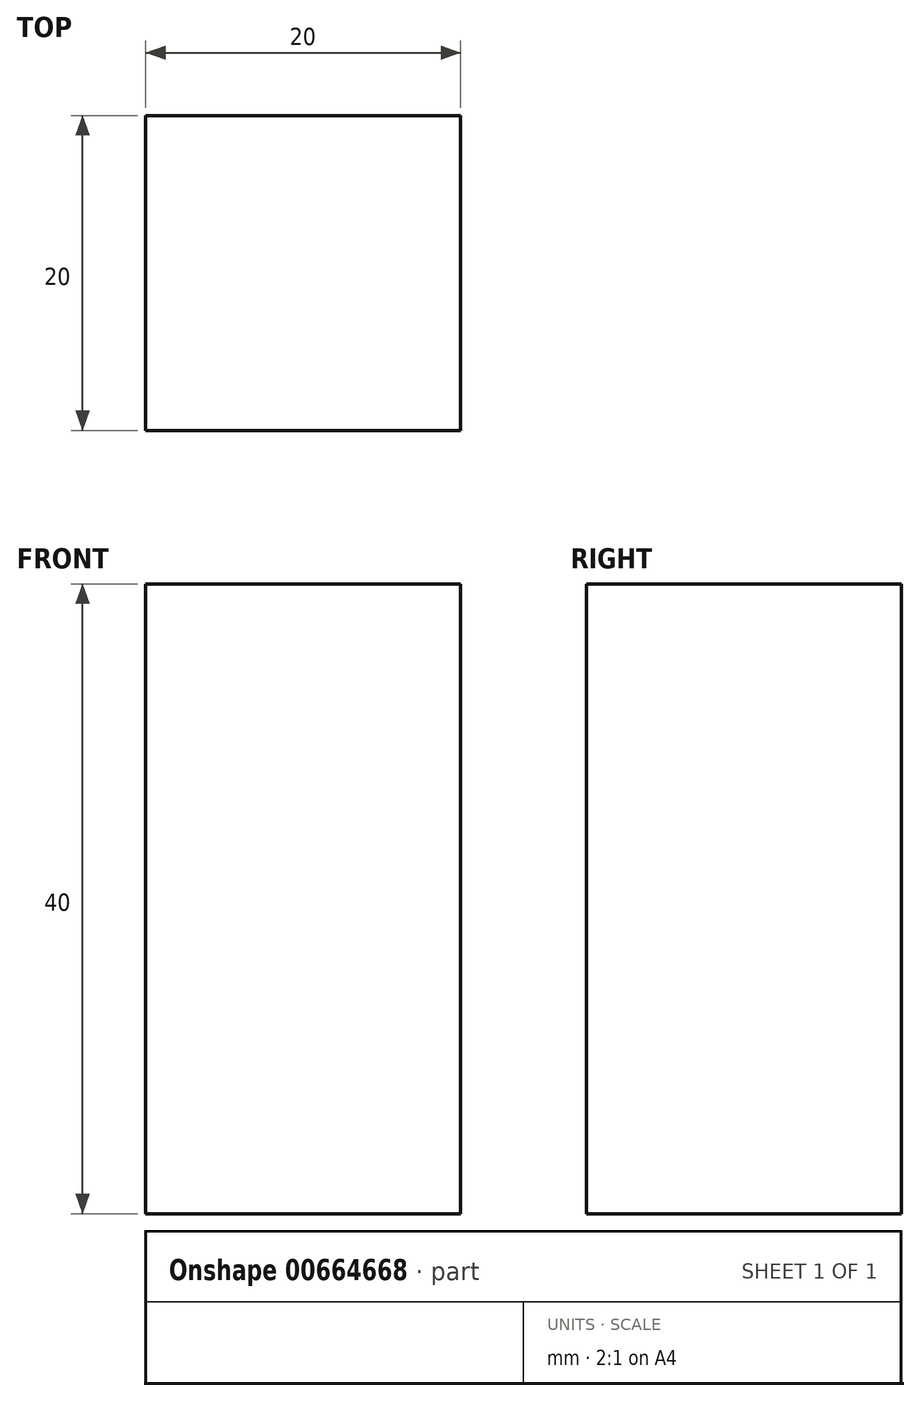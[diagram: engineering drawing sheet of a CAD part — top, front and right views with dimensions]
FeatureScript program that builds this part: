
annotation { "Feature Type Name" : "Feature", "Feature Type Description" : "" }
export const myFeature = defineFeature(function(context is Context, id is Id, definition is map)
    precondition{}
    {
        {
            var Q0;
            Q0=qCreatedBy(makeId("Top.planeOp"),FACE);
            var sketch = newSketch(context, id + "F0", { "sketchPlane" : qUnion([Q0])});
            skLineSegment(sketch, "E0.bottom", {"start": v(-113.61, -5.44) * mm, "end": v(-93.61, -5.44) * mm});
            skLineSegment(sketch, "E0.top", {"start": v(-113.61, -25.44) * mm, "end": v(-93.61, -25.44) * mm});
            skLineSegment(sketch, "E0.left", {"start": v(-113.61, -5.44) * mm, "end": v(-113.61, -25.44) * mm});
            skLineSegment(sketch, "E0.right", {"start": v(-93.61, -5.44) * mm, "end": v(-93.61, -25.44) * mm});
            skSolve(sketch);
        }
        {
            var Q0;
            Q0=makeQuery(id+"F0.imprint","IMPRINT",FACE,{"disambiguationData":[TD([[makeQuery(id+"F0.imprint","IMPRINT",EDGE,{"derivedFrom":sQuery(id+"F0.wireOp",EDGE,"E0.bottom")}),-1.0]])]});
            extrude(context, id + "F1", {"entities" : qUnion([Q0]), "depth" : 40 * mm, "offsetDistance" : 25.4 * mm});
        }
    });
